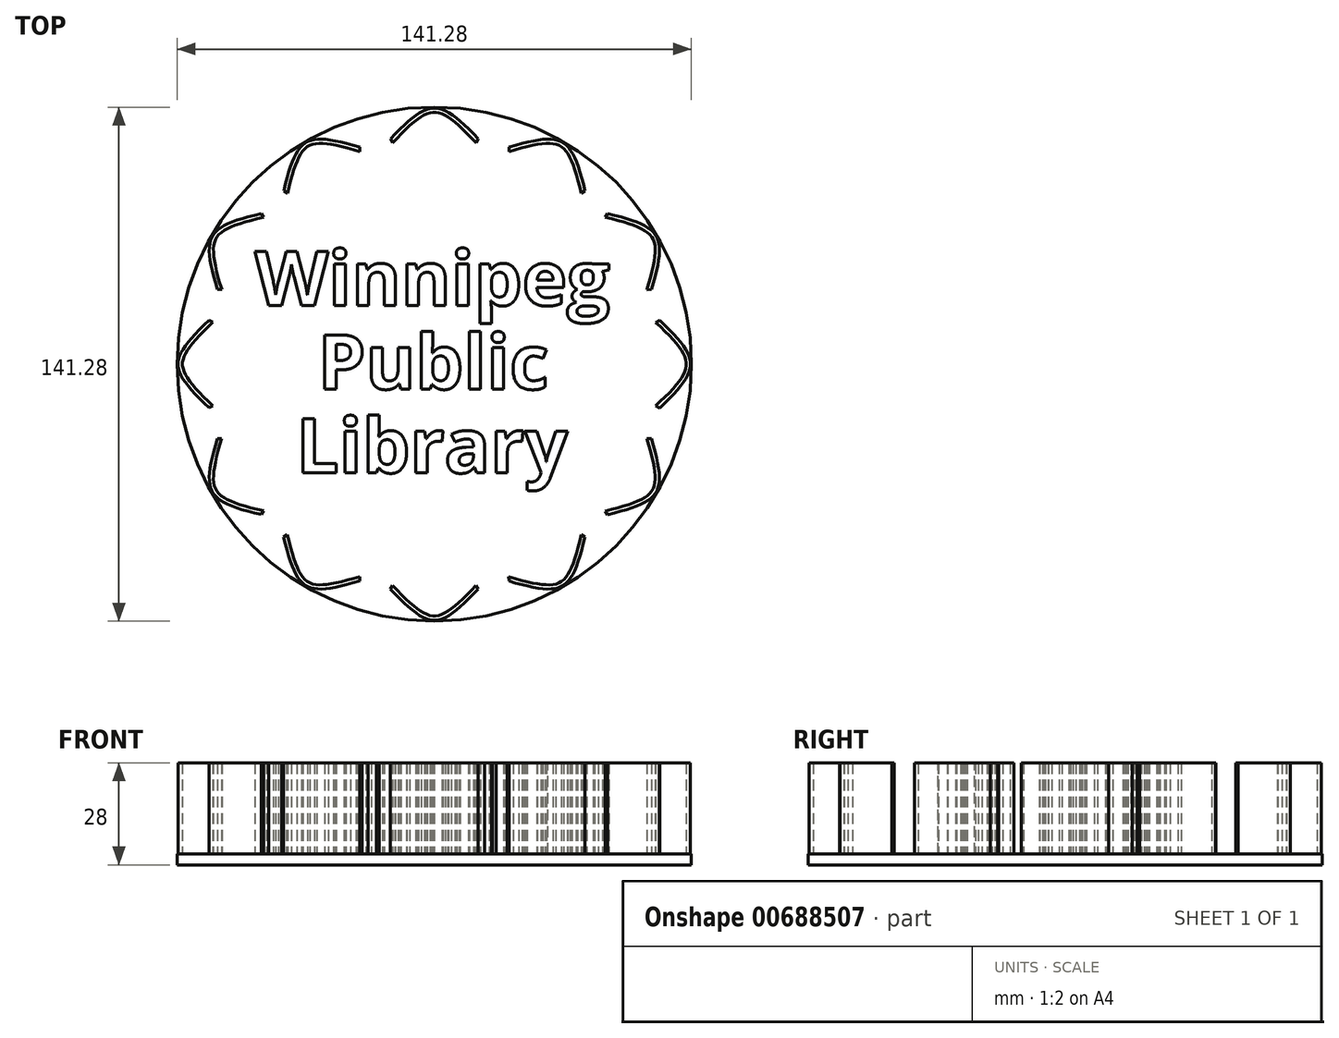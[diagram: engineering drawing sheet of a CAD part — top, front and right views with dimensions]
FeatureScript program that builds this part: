
annotation { "Feature Type Name" : "Feature", "Feature Type Description" : "" }
export const myFeature = defineFeature(function(context is Context, id is Id, definition is map)
    precondition{}
    {
        {
            var Q0;
            Q0=qCreatedBy(makeId("Top.planeOp"),FACE);
            var sketch = newSketch(context, id + "F0", { "sketchPlane" : qUnion([Q0])});
            skCircle(sketch, "E0", {"center": v(0, 0) * mm, "radius": 40 * mm, "construction": true});
            skCircle(sketch, "E1", {"center": v(0, 0) * mm, "radius": 58.7 * mm});
            skFitSpline(sketch, "E2", {"points": [v(-17.38, 56.08) * mm, v(17.45, 56.06) * mm], "startDerivative": vector(52.13, 57.12) * mm, "endDerivative": vector(52.34, -57.19) * mm});
            skFitSpline(sketch, "E3.0", {"points": [v(-16.5, 55.27) * mm, v(-14.32, 57.65) * mm, v(-10.53, 61.8) * mm, v(-6.84, 65.47) * mm, v(-4.38, 67.46) * mm, v(-2.74, 68.47) * mm, v(-1.3, 69.04) * mm, v(0, 69.22) * mm, v(1.31, 69.04) * mm, v(2.76, 68.47) * mm, v(4.4, 67.45) * mm, v(6.88, 65.46) * mm, v(10.57, 61.8) * mm, v(14.38, 57.63) * mm, v(16.56, 55.25) * mm]});
            skSolve(sketch);
        }
        {
            var Q0;
            Q0=qCreatedBy(makeId("Front.planeOp"),FACE);
            var sketch = newSketch(context, id + "F1", { "sketchPlane" : qUnion([Q0])});
            skLineSegment(sketch, "E4", {"start": v(0, 0) * mm, "end": v(0, 34.43) * mm, "construction": true});
            skSolve(sketch);
        }
        {
            var Q0;
            {var subQ0=sQuery(id+"F0.wireOp",EDGE,"E2");Q0=makeQuery(id+"F0.imprint","IMPRINT",FACE,{"disambiguationData":[TD([[makeQuery(id+"F0.imprint","IMPRINT",EDGE,{"derivedFrom":subQ0}),-1.0]])]});}
            extrude(context, id + "F2", {"entities" : qUnion([Q0]), "depth" : 25 * mm, "offsetDistance" : 25 * mm});
        }
        {
            var Q0;
            Q0=makeQuery(id+"F2.opExtrude","SWEPT_BODY",BODY,{"disambiguationData":[OSD([sQuery(id+"F0.wireOp",EDGE,"E2"),sQuery(id+"F0.wireOp",EDGE,"E1"),sQuery(id+"F0.wireOp",EDGE,"E3.0")])]});
            var Q1;
            Q1=sQuery(id+"F1.wireOp",EDGE,"E4");
            circularPattern(context, id + "F3", {"entities" : qUnion([Q0]), "axis" : qUnion([Q1]), "angle" : 360 * degree, "instanceCount" : 12, "equalSpace" : true});
        }
        {
            var Q0;
            {var subQ0=sQuery(id+"F0.wireOp",EDGE,"E1");var subQ1=sQuery(id+"F0.wireOp",EDGE,"E2");Q0=makeQuery(id+"F2.opExtrude","SWEPT_EDGE",EDGE,{"disambiguationData":[OSD([subQ1,subQ0]),TDD([makeQuery(id+"F0.imprint","INTERSECT",VERTEX,{"disambiguationData":[OD(1.0)],"derivedFrom":[subQ1,subQ0]})])]});}
            var Q1;
            {var subQ0=sQuery(id+"F0.wireOp",EDGE,"E1");var subQ1=sQuery(id+"F0.wireOp",EDGE,"E2");Q1=makeQuery(id+"F3.opPattern","COPY",EDGE,{"derivedFrom":makeQuery(id+"F2.opExtrude","SWEPT_EDGE",EDGE,{"disambiguationData":[OSD([subQ1,subQ0]),TDD([makeQuery(id+"F0.imprint","INTERSECT",VERTEX,{"disambiguationData":[OD(0.0)],"derivedFrom":[subQ1,subQ0]})])]}),"instanceName":"11"});}
            var Q2;
            {var subQ0=sQuery(id+"F0.wireOp",EDGE,"E1");var subQ1=sQuery(id+"F0.wireOp",EDGE,"E2");Q2=makeQuery(id+"F3.opPattern","COPY",EDGE,{"derivedFrom":makeQuery(id+"F2.opExtrude","SWEPT_EDGE",EDGE,{"disambiguationData":[OSD([subQ1,subQ0]),TDD([makeQuery(id+"F0.imprint","INTERSECT",VERTEX,{"disambiguationData":[OD(0.0)],"derivedFrom":[subQ1,subQ0]})])]}),"instanceName":"10"});}
            var Q3;
            {var subQ0=sQuery(id+"F0.wireOp",EDGE,"E1");var subQ1=sQuery(id+"F0.wireOp",EDGE,"E2");Q3=makeQuery(id+"F3.opPattern","COPY",EDGE,{"derivedFrom":makeQuery(id+"F2.opExtrude","SWEPT_EDGE",EDGE,{"disambiguationData":[OSD([subQ1,subQ0]),TDD([makeQuery(id+"F0.imprint","INTERSECT",VERTEX,{"disambiguationData":[OD(1.0)],"derivedFrom":[subQ1,subQ0]})])]}),"instanceName":"11"});}
            var Q4;
            {var subQ0=sQuery(id+"F0.wireOp",EDGE,"E1");var subQ1=sQuery(id+"F0.wireOp",EDGE,"E2");Q4=makeQuery(id+"F3.opPattern","COPY",EDGE,{"derivedFrom":makeQuery(id+"F2.opExtrude","SWEPT_EDGE",EDGE,{"disambiguationData":[OSD([subQ1,subQ0]),TDD([makeQuery(id+"F0.imprint","INTERSECT",VERTEX,{"disambiguationData":[OD(0.0)],"derivedFrom":[subQ1,subQ0]})])]}),"instanceName":"9"});}
            var Q5;
            {var subQ0=sQuery(id+"F0.wireOp",EDGE,"E1");var subQ1=sQuery(id+"F0.wireOp",EDGE,"E2");Q5=makeQuery(id+"F3.opPattern","COPY",EDGE,{"derivedFrom":makeQuery(id+"F2.opExtrude","SWEPT_EDGE",EDGE,{"disambiguationData":[OSD([subQ1,subQ0]),TDD([makeQuery(id+"F0.imprint","INTERSECT",VERTEX,{"disambiguationData":[OD(1.0)],"derivedFrom":[subQ1,subQ0]})])]}),"instanceName":"10"});}
            var Q6;
            {var subQ0=sQuery(id+"F0.wireOp",EDGE,"E1");var subQ1=sQuery(id+"F0.wireOp",EDGE,"E2");Q6=makeQuery(id+"F2.opExtrude","SWEPT_EDGE",EDGE,{"disambiguationData":[OSD([subQ1,subQ0]),TDD([makeQuery(id+"F0.imprint","INTERSECT",VERTEX,{"disambiguationData":[OD(0.0)],"derivedFrom":[subQ1,subQ0]})])]});}
            var Q7;
            {var subQ0=sQuery(id+"F0.wireOp",EDGE,"E1");var subQ1=sQuery(id+"F0.wireOp",EDGE,"E2");Q7=makeQuery(id+"F3.opPattern","COPY",EDGE,{"derivedFrom":makeQuery(id+"F2.opExtrude","SWEPT_EDGE",EDGE,{"disambiguationData":[OSD([subQ1,subQ0]),TDD([makeQuery(id+"F0.imprint","INTERSECT",VERTEX,{"disambiguationData":[OD(1.0)],"derivedFrom":[subQ1,subQ0]})])]}),"instanceName":"1"});}
            var Q8;
            {var subQ0=sQuery(id+"F0.wireOp",EDGE,"E1");var subQ1=sQuery(id+"F0.wireOp",EDGE,"E2");Q8=makeQuery(id+"F3.opPattern","COPY",EDGE,{"derivedFrom":makeQuery(id+"F2.opExtrude","SWEPT_EDGE",EDGE,{"disambiguationData":[OSD([subQ1,subQ0]),TDD([makeQuery(id+"F0.imprint","INTERSECT",VERTEX,{"disambiguationData":[OD(0.0)],"derivedFrom":[subQ1,subQ0]})])]}),"instanceName":"1"});}
            var Q9;
            {var subQ0=sQuery(id+"F0.wireOp",EDGE,"E1");var subQ1=sQuery(id+"F0.wireOp",EDGE,"E2");Q9=makeQuery(id+"F3.opPattern","COPY",EDGE,{"derivedFrom":makeQuery(id+"F2.opExtrude","SWEPT_EDGE",EDGE,{"disambiguationData":[OSD([subQ1,subQ0]),TDD([makeQuery(id+"F0.imprint","INTERSECT",VERTEX,{"disambiguationData":[OD(0.0)],"derivedFrom":[subQ1,subQ0]})])]}),"instanceName":"8"});}
            var Q10;
            {var subQ0=sQuery(id+"F0.wireOp",EDGE,"E1");var subQ1=sQuery(id+"F0.wireOp",EDGE,"E2");Q10=makeQuery(id+"F3.opPattern","COPY",EDGE,{"derivedFrom":makeQuery(id+"F2.opExtrude","SWEPT_EDGE",EDGE,{"disambiguationData":[OSD([subQ1,subQ0]),TDD([makeQuery(id+"F0.imprint","INTERSECT",VERTEX,{"disambiguationData":[OD(1.0)],"derivedFrom":[subQ1,subQ0]})])]}),"instanceName":"9"});}
            var Q11;
            {var subQ0=sQuery(id+"F0.wireOp",EDGE,"E1");var subQ1=sQuery(id+"F0.wireOp",EDGE,"E2");Q11=makeQuery(id+"F3.opPattern","COPY",EDGE,{"derivedFrom":makeQuery(id+"F2.opExtrude","SWEPT_EDGE",EDGE,{"disambiguationData":[OSD([subQ1,subQ0]),TDD([makeQuery(id+"F0.imprint","INTERSECT",VERTEX,{"disambiguationData":[OD(1.0)],"derivedFrom":[subQ1,subQ0]})])]}),"instanceName":"2"});}
            var Q12;
            {var subQ0=sQuery(id+"F0.wireOp",EDGE,"E1");var subQ1=sQuery(id+"F0.wireOp",EDGE,"E2");Q12=makeQuery(id+"F3.opPattern","COPY",EDGE,{"derivedFrom":makeQuery(id+"F2.opExtrude","SWEPT_EDGE",EDGE,{"disambiguationData":[OSD([subQ1,subQ0]),TDD([makeQuery(id+"F0.imprint","INTERSECT",VERTEX,{"disambiguationData":[OD(1.0)],"derivedFrom":[subQ1,subQ0]})])]}),"instanceName":"3"});}
            var Q13;
            {var subQ0=sQuery(id+"F0.wireOp",EDGE,"E1");var subQ1=sQuery(id+"F0.wireOp",EDGE,"E2");Q13=makeQuery(id+"F3.opPattern","COPY",EDGE,{"derivedFrom":makeQuery(id+"F2.opExtrude","SWEPT_EDGE",EDGE,{"disambiguationData":[OSD([subQ1,subQ0]),TDD([makeQuery(id+"F0.imprint","INTERSECT",VERTEX,{"disambiguationData":[OD(0.0)],"derivedFrom":[subQ1,subQ0]})])]}),"instanceName":"2"});}
            var Q14;
            {var subQ0=sQuery(id+"F0.wireOp",EDGE,"E1");var subQ1=sQuery(id+"F0.wireOp",EDGE,"E2");Q14=makeQuery(id+"F3.opPattern","COPY",EDGE,{"derivedFrom":makeQuery(id+"F2.opExtrude","SWEPT_EDGE",EDGE,{"disambiguationData":[OSD([subQ1,subQ0]),TDD([makeQuery(id+"F0.imprint","INTERSECT",VERTEX,{"disambiguationData":[OD(1.0)],"derivedFrom":[subQ1,subQ0]})])]}),"instanceName":"4"});}
            var Q15;
            {var subQ0=sQuery(id+"F0.wireOp",EDGE,"E1");var subQ1=sQuery(id+"F0.wireOp",EDGE,"E2");Q15=makeQuery(id+"F3.opPattern","COPY",EDGE,{"derivedFrom":makeQuery(id+"F2.opExtrude","SWEPT_EDGE",EDGE,{"disambiguationData":[OSD([subQ1,subQ0]),TDD([makeQuery(id+"F0.imprint","INTERSECT",VERTEX,{"disambiguationData":[OD(0.0)],"derivedFrom":[subQ1,subQ0]})])]}),"instanceName":"3"});}
            var Q16;
            {var subQ0=sQuery(id+"F0.wireOp",EDGE,"E1");var subQ1=sQuery(id+"F0.wireOp",EDGE,"E2");Q16=makeQuery(id+"F3.opPattern","COPY",EDGE,{"derivedFrom":makeQuery(id+"F2.opExtrude","SWEPT_EDGE",EDGE,{"disambiguationData":[OSD([subQ1,subQ0]),TDD([makeQuery(id+"F0.imprint","INTERSECT",VERTEX,{"disambiguationData":[OD(1.0)],"derivedFrom":[subQ1,subQ0]})])]}),"instanceName":"5"});}
            var Q17;
            {var subQ0=sQuery(id+"F0.wireOp",EDGE,"E1");var subQ1=sQuery(id+"F0.wireOp",EDGE,"E2");Q17=makeQuery(id+"F3.opPattern","COPY",EDGE,{"derivedFrom":makeQuery(id+"F2.opExtrude","SWEPT_EDGE",EDGE,{"disambiguationData":[OSD([subQ1,subQ0]),TDD([makeQuery(id+"F0.imprint","INTERSECT",VERTEX,{"disambiguationData":[OD(0.0)],"derivedFrom":[subQ1,subQ0]})])]}),"instanceName":"4"});}
            var Q18;
            {var subQ0=sQuery(id+"F0.wireOp",EDGE,"E1");var subQ1=sQuery(id+"F0.wireOp",EDGE,"E2");Q18=makeQuery(id+"F3.opPattern","COPY",EDGE,{"derivedFrom":makeQuery(id+"F2.opExtrude","SWEPT_EDGE",EDGE,{"disambiguationData":[OSD([subQ1,subQ0]),TDD([makeQuery(id+"F0.imprint","INTERSECT",VERTEX,{"disambiguationData":[OD(1.0)],"derivedFrom":[subQ1,subQ0]})])]}),"instanceName":"6"});}
            var Q19;
            {var subQ0=sQuery(id+"F0.wireOp",EDGE,"E1");var subQ1=sQuery(id+"F0.wireOp",EDGE,"E2");Q19=makeQuery(id+"F3.opPattern","COPY",EDGE,{"derivedFrom":makeQuery(id+"F2.opExtrude","SWEPT_EDGE",EDGE,{"disambiguationData":[OSD([subQ1,subQ0]),TDD([makeQuery(id+"F0.imprint","INTERSECT",VERTEX,{"disambiguationData":[OD(0.0)],"derivedFrom":[subQ1,subQ0]})])]}),"instanceName":"5"});}
            var Q20;
            {var subQ0=sQuery(id+"F0.wireOp",EDGE,"E1");var subQ1=sQuery(id+"F0.wireOp",EDGE,"E2");Q20=makeQuery(id+"F3.opPattern","COPY",EDGE,{"derivedFrom":makeQuery(id+"F2.opExtrude","SWEPT_EDGE",EDGE,{"disambiguationData":[OSD([subQ1,subQ0]),TDD([makeQuery(id+"F0.imprint","INTERSECT",VERTEX,{"disambiguationData":[OD(1.0)],"derivedFrom":[subQ1,subQ0]})])]}),"instanceName":"7"});}
            var Q21;
            {var subQ0=sQuery(id+"F0.wireOp",EDGE,"E1");var subQ1=sQuery(id+"F0.wireOp",EDGE,"E2");Q21=makeQuery(id+"F3.opPattern","COPY",EDGE,{"derivedFrom":makeQuery(id+"F2.opExtrude","SWEPT_EDGE",EDGE,{"disambiguationData":[OSD([subQ1,subQ0]),TDD([makeQuery(id+"F0.imprint","INTERSECT",VERTEX,{"disambiguationData":[OD(0.0)],"derivedFrom":[subQ1,subQ0]})])]}),"instanceName":"6"});}
            var Q22;
            {var subQ0=sQuery(id+"F0.wireOp",EDGE,"E1");var subQ1=sQuery(id+"F0.wireOp",EDGE,"E2");Q22=makeQuery(id+"F3.opPattern","COPY",EDGE,{"derivedFrom":makeQuery(id+"F2.opExtrude","SWEPT_EDGE",EDGE,{"disambiguationData":[OSD([subQ1,subQ0]),TDD([makeQuery(id+"F0.imprint","INTERSECT",VERTEX,{"disambiguationData":[OD(0.0)],"derivedFrom":[subQ1,subQ0]})])]}),"instanceName":"7"});}
            var Q23;
            {var subQ0=sQuery(id+"F0.wireOp",EDGE,"E1");var subQ1=sQuery(id+"F0.wireOp",EDGE,"E2");Q23=makeQuery(id+"F3.opPattern","COPY",EDGE,{"derivedFrom":makeQuery(id+"F2.opExtrude","SWEPT_EDGE",EDGE,{"disambiguationData":[OSD([subQ1,subQ0]),TDD([makeQuery(id+"F0.imprint","INTERSECT",VERTEX,{"disambiguationData":[OD(1.0)],"derivedFrom":[subQ1,subQ0]})])]}),"instanceName":"8"});}
            chamfer(context, id + "F4", {"entities" : qUnion([Q0, Q1, Q2, Q3, Q4, Q5, Q6, Q7, Q8, Q9, Q10, Q11, Q12, Q13, Q14, Q15, Q16, Q17, Q18, Q19, Q20, Q21, Q22, Q23]), "width" : 2.4 * mm, "tangentPropagation" : true});
        }
        {
            var Q0;
            Q0=qCreatedBy(makeId("Top.planeOp"),FACE);
            var sketch = newSketch(context, id + "F5", { "sketchPlane" : qUnion([Q0])});
            skCircle(sketch, "E5", {"center": v(0, 0) * mm, "radius": 70.64 * mm});
            skSolve(sketch);
        }
        {
            var Q0;
            Q0=makeQuery(id+"F5.imprint","IMPRINT",FACE,{"disambiguationData":[TD([[makeQuery(id+"F5.imprint","IMPRINT",EDGE,{"derivedFrom":sQuery(id+"F5.wireOp",EDGE,"E5")}),1.0]])]});
            extrude(context, id + "F6", {"entities" : qUnion([Q0]), "oppositeDirection" : true, "depth" : 3 * mm, "offsetDistance" : 25 * mm});
        }
        {
            var Q0;
            Q0=makeQuery(id+"F6.opExtrude","CAP_FACE",FACE,{"disambiguationData":[OSD([sQuery(id+"F5.wireOp",EDGE,"E5")])],"isStart":true});
            var sketch = newSketch(context, id + "F7", { "sketchPlane" : qUnion([Q0])});
            skText(sketch, "E6", { "text": "Winnipeg", "fontName": "OpenSans-Bold.ttf"});
            skText(sketch, "E7", { "text": "Public", "fontName": "OpenSans-Bold.ttf"});
            skText(sketch, "E8", { "text": "Library", "fontName": "OpenSans-Bold.ttf"});
            const initialGuessF7  = {"E6": [-0.0493, 0.01612, 1, 0, 0.015], "E7": [-0.03197, -0.00688, 1, 0, 0.015], "E8": [-0.038, -0.02988, 1, 0, 0.015]};
            skSetInitialGuess(sketch, initialGuessF7);
            skSolve(sketch);
        }
        {
            var Q0;
            Q0=makeQuery(id+"F7.imprint","IMPRINT",FACE,{"disambiguationData":[TD([[makeQuery(id+"F7.imprint","IMPRINT",EDGE,{"derivedFrom":sQuery(id+"F7.wireOp",EDGE,"E6.sketch_text.stroke-0")}),-1.0]])]});
            var Q1;
            Q1=makeQuery(id+"F7.imprint","IMPRINT",FACE,{"disambiguationData":[TD([[makeQuery(id+"F7.imprint","IMPRINT",EDGE,{"derivedFrom":sQuery(id+"F7.wireOp",EDGE,"E6.sketch_text.stroke-29")}),-1.0]])]});
            var Q2;
            Q2 = qSketchRegion(id + "F7", true);
            extrude(context, id + "F8", {"entities" : qUnion([Q0, Q1, Q2]), "operationType" : NewBodyOperationType.ADD, "depth" : 25 * mm, "offsetDistance" : 25 * mm});
        }
    });
